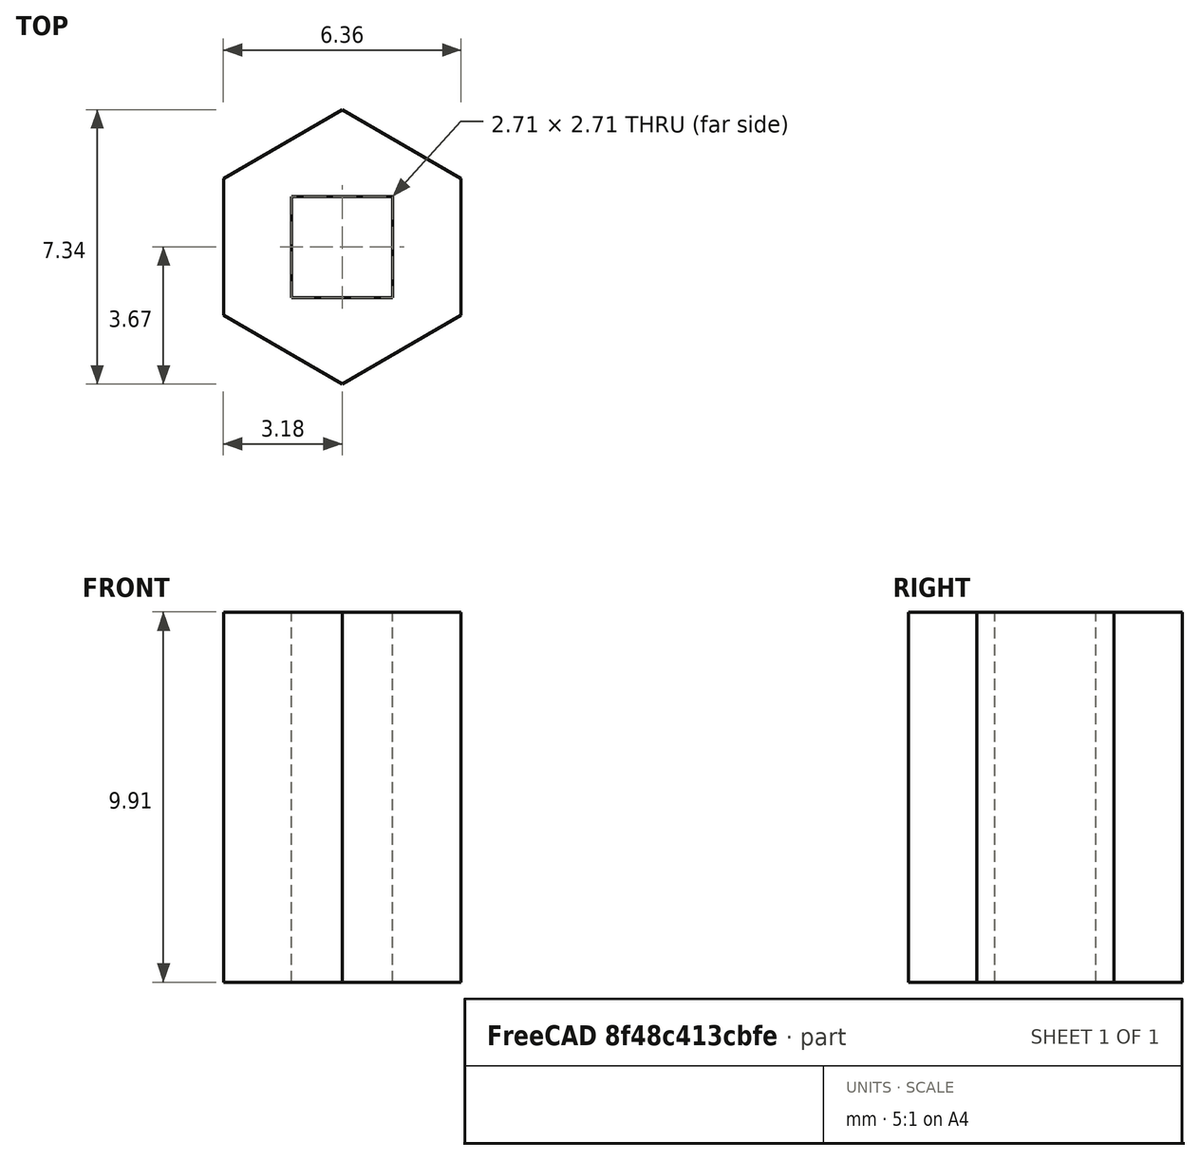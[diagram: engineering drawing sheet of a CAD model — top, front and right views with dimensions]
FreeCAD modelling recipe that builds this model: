
FCSTD DOCUMENT  (FreeCAD 1.0R39109 (Git))
Label: M3 Tap adapter
License: All rights reserved
LicenseURL: https://en.wikipedia.org/wiki/All_rights_reserved
objects: Sketcher::SketchObject×1, PartDesign::Pad×1, PartDesign::Body×1
note: 6 computed .brp shape members not serialized (recipe doc carries the construction recipe); baked Part::Feature solids carry a one-line shape summary decoded from their .brp

FEATURE [Sketcher::SketchObject] Sketch
  ArcFitTolerance = 1e-06
  AttachmentSupport = -> [XY_Plane]
  FullyConstrained = true
  MakeInternals = false
  MapMode = 5
  sketch-geometry (12):
    g0: LineSegment StartX=0 StartY=3.66617 StartZ=0 EndX=-3.175 EndY=1.83309 EndZ=0
    g1: LineSegment StartX=-3.175 StartY=1.83309 StartZ=0 EndX=-3.175 EndY=-1.83309 EndZ=0
    g2: LineSegment StartX=-3.175 StartY=-1.83309 StartZ=0 EndX=-4e-16 EndY=-3.66617 EndZ=0
    g3: LineSegment StartX=-4e-16 StartY=-3.66617 StartZ=0 EndX=3.175 EndY=-1.83309 EndZ=0
    g4: LineSegment StartX=3.175 StartY=-1.83309 StartZ=0 EndX=3.175 EndY=1.83309 EndZ=0
    g5: LineSegment StartX=3.175 StartY=1.83309 StartZ=0 EndX=0 EndY=3.66617 EndZ=0
    g6: Circle [constr] CenterX=0 CenterY=1e-16 CenterZ=0 NormalX=0 NormalY=0 NormalZ=1 AngleXU=0 Radius=3.66617
    g7: LineSegment StartX=-1.35255 StartY=-1.35255 StartZ=0 EndX=1.35255 EndY=-1.35255 EndZ=0
    g8: LineSegment StartX=1.35255 StartY=-1.35255 StartZ=0 EndX=1.35255 EndY=1.35255 EndZ=0
    g9: LineSegment StartX=1.35255 StartY=1.35255 StartZ=0 EndX=-1.35255 EndY=1.35255 EndZ=0
    g10: LineSegment StartX=-1.35255 StartY=1.35255 StartZ=0 EndX=-1.35255 EndY=-1.35255 EndZ=0
    g11: GeomPoint [constr] X=0 Y=1e-16 Z=0
  constraints (28):
    c: Coincident(g0,g1)
    c: Coincident(g1,g2)
    c: Coincident(g2,g3)
    c: Coincident(g3,g4)
    c: Coincident(g4,g5)
    c: Coincident(g5,g0)
    c: Equal(g0, g1-g5) x5
    c: PointOnObject(g0,g6)
    c: PointOnObject(g1,g6)
    c: PointOnObject(g2,g6)
    c: PointOnObject(g3,g6)
    c: PointOnObject(g4,g6)
    c: PointOnObject(g5,g6)
    c: Coincident(g6,g-1)
    c: PointOnObject(g5,g-2)
    c: Distance(g4,g1) = 6.35
    c: Coincident(g7,g8)
    c: Coincident(g8,g9)
    c: Coincident(g9,g10)
    c: Coincident(g10,g7)
    c: Horizontal(g7)
    c: Horizontal(g9)
    c: Vertical(g8)
    c: Vertical(g10)
    c: Symmetric(g9,g7,g11)
    c: Coincident(g11,g6)
    c: DistanceX(g7,g7) = 2.7051
    c: Equal(g7,g8)
FEATURE [PartDesign::Pad] Pad
  Direction = (0,0,1)
  Length = 9.906
  Length2 = 10
  Profile = -> Sketch
  ReferenceAxis = -> Sketch [N_Axis]
  Refine = true
  Suppressed = false
  Type = 0
FEATURE [PartDesign::Body] Body
  AllowCompound = false
  Group = -> [Sketch,Pad]
  Origin = -> Origin
  Tip = -> Pad
